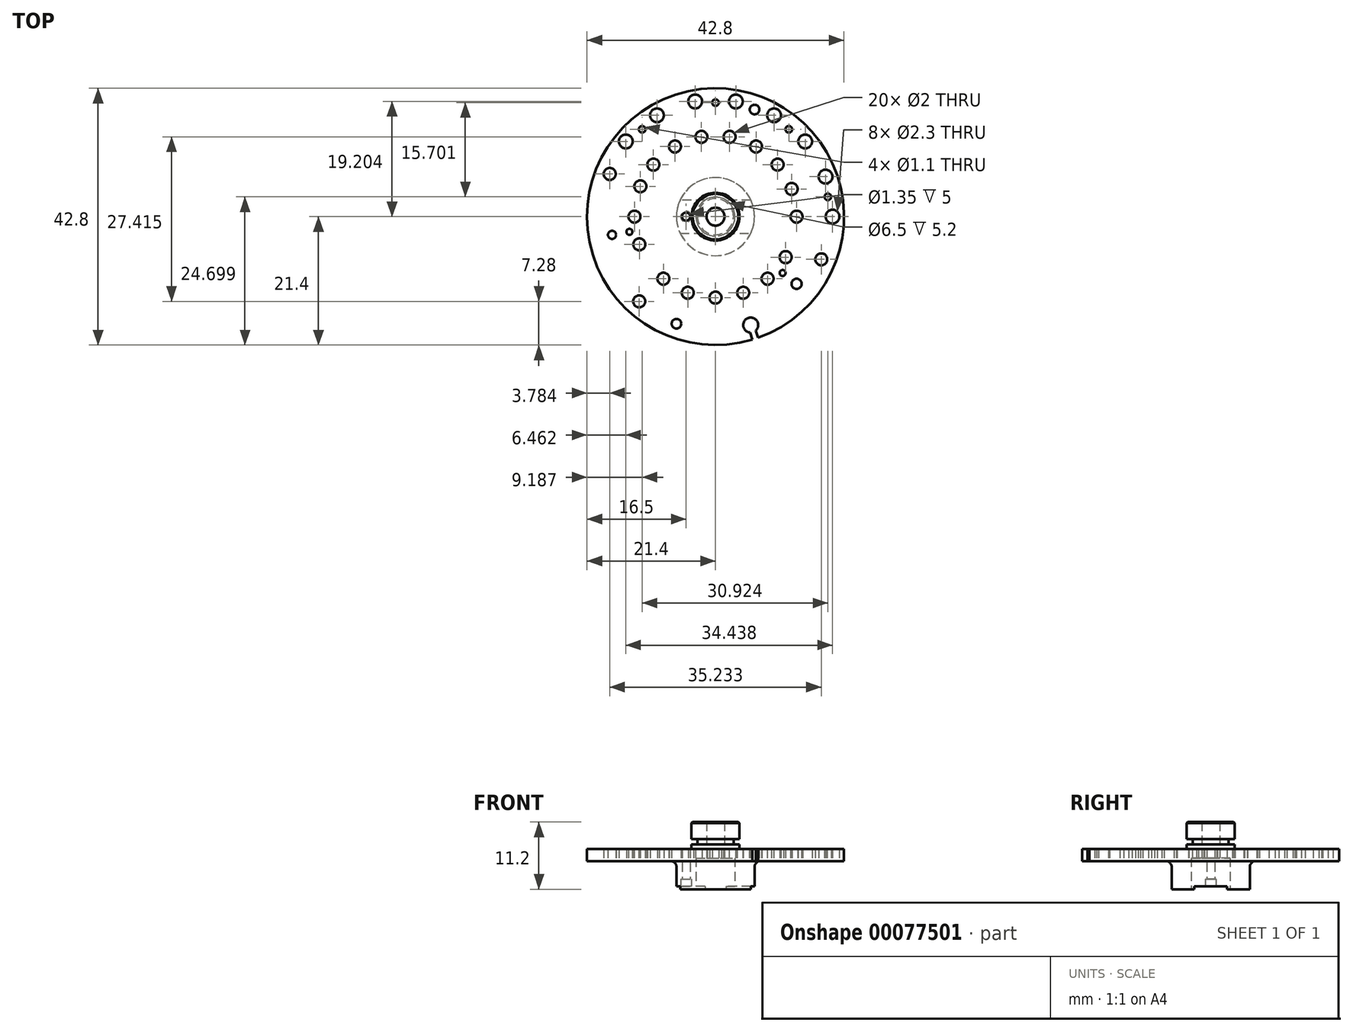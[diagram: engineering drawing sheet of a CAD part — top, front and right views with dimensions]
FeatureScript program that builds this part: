
annotation { "Feature Type Name" : "Feature", "Feature Type Description" : "" }
export const myFeature = defineFeature(function(context is Context, id is Id, definition is map)
    precondition{}
    {
        {
            var Q0;
            Q0=qCreatedBy(makeId("Front.planeOp"),FACE);
            var sketch = newSketch(context, id + "F0", { "sketchPlane" : qUnion([Q0])});
            skLineSegment(sketch, "E0", {"start": v(3.25, 0) * mm, "end": v(6.5, 0) * mm});
            skLineSegment(sketch, "E1", {"start": v(6.5, 0) * mm, "end": v(6.5, 4.7) * mm});
            skLineSegment(sketch, "E2", {"start": v(6.5, 4.7) * mm, "end": v(21.4, 4.7) * mm});
            skLineSegment(sketch, "E3", {"start": v(21.4, 4.7) * mm, "end": v(21.4, 6.7) * mm});
            skLineSegment(sketch, "E4", {"start": v(21.4, 6.7) * mm, "end": v(4, 6.7) * mm});
            skLineSegment(sketch, "E5", {"start": v(4, 6.7) * mm, "end": v(4, 7.5) * mm});
            skLineSegment(sketch, "E6", {"start": v(4, 11.2) * mm, "end": v(1.5, 11.2) * mm});
            skLineSegment(sketch, "E7", {"start": v(1.5, 11.2) * mm, "end": v(1.5, 5.2) * mm});
            skLineSegment(sketch, "E8", {"start": v(1.5, 5.2) * mm, "end": v(3.25, 5.2) * mm});
            skLineSegment(sketch, "E9", {"start": v(3.25, 5.2) * mm, "end": v(3.25, 0) * mm});
            skLineSegment(sketch, "E10", {"start": v(4, 7.5) * mm, "end": v(3, 7.5) * mm});
            skLineSegment(sketch, "E11", {"start": v(3, 7.5) * mm, "end": v(3, 8.35) * mm});
            skLineSegment(sketch, "E12", {"start": v(3, 8.35) * mm, "end": v(4, 8.35) * mm});
            skLineSegment(sketch, "E13", {"start": v(4, 8.35) * mm, "end": v(4, 11.2) * mm});
            skLineSegment(sketch, "E14", {"start": v(0, 0) * mm, "end": v(0, 11.2) * mm, "construction": true});
            skSolve(sketch);
        }
        {
            var Q0;
            Q0=makeQuery(id+"F0.imprint","IMPRINT",FACE,{"disambiguationData":[TD([[makeQuery(id+"F0.imprint","IMPRINT",EDGE,{"derivedFrom":sQuery(id+"F0.wireOp",EDGE,"E0")}),1.0]])]});
            var Q1;
            Q1=sQuery(id+"F0.wireOp",EDGE,"E14");
            revolve(context, id + "F1", {"entities" : qUnion([Q0]), "axis" : qUnion([Q1]), "revolveType" : RevolveType.FULL});
        }
        {
            var Q0;
            Q0=makeQuery(id+"F1.opRevolve","SWEPT_FACE",FACE,{"disambiguationData":[OSD([sQuery(id+"F0.wireOp",EDGE,"E2")])]});
            var sketch = newSketch(context, id + "F2", { "sketchPlane" : qUnion([Q0]), "disableImprinting" : false});
            skLineSegment(sketch, "E15", {"start": v(21.4, 0) * mm, "end": v(0, 0) * mm, "construction": true});
            skLineSegment(sketch, "E16", {"start": v(0, 0) * mm, "end": v(20.1, -7.32) * mm, "construction": true});
            skLineSegment(sketch, "E17", {"start": v(0, 0) * mm, "end": v(16.4, -13.76) * mm, "construction": true});
            skLineSegment(sketch, "E18", {"start": v(0, 0) * mm, "end": v(10.7, -18.53) * mm, "construction": true});
            skLineSegment(sketch, "E19", {"start": v(0, 0) * mm, "end": v(3.72, -21.07) * mm, "construction": true});
            skLineSegment(sketch, "E20", {"start": v(0, 0) * mm, "end": v(-3.72, -21.07) * mm, "construction": true});
            skLineSegment(sketch, "E21", {"start": v(0, 0) * mm, "end": v(-10.7, -18.53) * mm, "construction": true});
            skLineSegment(sketch, "E22", {"start": v(0, 0) * mm, "end": v(-16.4, -13.76) * mm, "construction": true});
            skLineSegment(sketch, "E23", {"start": v(0, 0) * mm, "end": v(-19.84, -8.02) * mm, "construction": true});
            skLineSegment(sketch, "E24", {"start": v(0, 0) * mm, "end": v(-21.4, 0) * mm, "construction": true});
            skLineSegment(sketch, "E25", {"start": v(0, 0) * mm, "end": v(-20.1, 7.32) * mm, "construction": true});
            skLineSegment(sketch, "E26", {"start": v(0, 0) * mm, "end": v(18.53, 10.7) * mm, "construction": true});
            skLineSegment(sketch, "E27", {"start": v(0, 0) * mm, "end": v(13.76, 16.4) * mm, "construction": true});
            skLineSegment(sketch, "E28", {"start": v(0, 0) * mm, "end": v(7.32, 20.1) * mm, "construction": true});
            skLineSegment(sketch, "E29", {"start": v(0, 0) * mm, "end": v(0, 21.4) * mm, "construction": true});
            skLineSegment(sketch, "E30", {"start": v(0, 0) * mm, "end": v(-7.32, 20.1) * mm, "construction": true});
            skLineSegment(sketch, "E31", {"start": v(0, 0) * mm, "end": v(-13.76, 16.4) * mm, "construction": true});
            skCircle(sketch, "E32", {"center": v(0, 0) * mm, "radius": 19.5 * mm, "construction": true});
            skCircle(sketch, "E33", {"center": v(0, 0) * mm, "radius": 13.5 * mm, "construction": true});
            skCircle(sketch, "E34", {"center": v(19.5, 0) * mm, "radius": 1.15 * mm});
            skCircle(sketch, "E35", {"center": v(18.32, -6.67) * mm, "radius": 1.15 * mm});
            skCircle(sketch, "E36", {"center": v(14.94, -12.53) * mm, "radius": 1.15 * mm});
            skCircle(sketch, "E37", {"center": v(9.75, -16.89) * mm, "radius": 1.15 * mm});
            skCircle(sketch, "E38", {"center": v(3.39, -19.2) * mm, "radius": 1.15 * mm});
            skCircle(sketch, "E39", {"center": v(-3.39, -19.2) * mm, "radius": 1.15 * mm});
            skCircle(sketch, "E40", {"center": v(-9.75, -16.89) * mm, "radius": 1.15 * mm});
            skCircle(sketch, "E41", {"center": v(-14.94, -12.53) * mm, "radius": 1.15 * mm});
            skCircle(sketch, "E42", {"center": v(-17.62, -7.12) * mm, "radius": 1 * mm});
            skCircle(sketch, "E43", {"center": v(11.7, 6.75) * mm, "radius": 1 * mm});
            skCircle(sketch, "E44", {"center": v(8.68, 10.34) * mm, "radius": 1 * mm});
            skCircle(sketch, "E45", {"center": v(12.69, -4.62) * mm, "radius": 1 * mm});
            skCircle(sketch, "E46", {"center": v(13.5, 0) * mm, "radius": 1 * mm});
            skCircle(sketch, "E47", {"center": v(10.34, -8.68) * mm, "radius": 1 * mm});
            skCircle(sketch, "E48", {"center": v(6.75, -11.7) * mm, "radius": 1 * mm});
            skCircle(sketch, "E49", {"center": v(2.34, -13.3) * mm, "radius": 1 * mm});
            skCircle(sketch, "E50", {"center": v(-2.34, -13.3) * mm, "radius": 1 * mm});
            skCircle(sketch, "E51", {"center": v(-6.75, -11.7) * mm, "radius": 1 * mm});
            skCircle(sketch, "E52", {"center": v(-10.34, -8.68) * mm, "radius": 1 * mm});
            skCircle(sketch, "E53", {"center": v(-12.52, -5.06) * mm, "radius": 1 * mm});
            skCircle(sketch, "E54", {"center": v(-13.5, 0) * mm, "radius": 1 * mm});
            skCircle(sketch, "E55", {"center": v(-12.69, 4.62) * mm, "radius": 1 * mm});
            skCircle(sketch, "E56", {"center": v(-8.68, 10.34) * mm, "radius": 1 * mm});
            skCircle(sketch, "E57", {"center": v(-4.62, 12.69) * mm, "radius": 1 * mm});
            skCircle(sketch, "E58", {"center": v(0, 13.5) * mm, "radius": 1 * mm});
            skCircle(sketch, "E59", {"center": v(4.62, 12.69) * mm, "radius": 1 * mm});
            skLineSegment(sketch, "E60", {"start": v(0, 0) * mm, "end": v(21.07, -3.72) * mm, "construction": true});
            skLineSegment(sketch, "E61", {"start": v(0, 0) * mm, "end": v(13.76, -16.4) * mm, "construction": true});
            skLineSegment(sketch, "E62", {"start": v(0, 0) * mm, "end": v(7.32, -20.1) * mm, "construction": true});
            skLineSegment(sketch, "E63", {"start": v(0, 0) * mm, "end": v(0, -21.4) * mm, "construction": true});
            skLineSegment(sketch, "E64", {"start": v(0, 0) * mm, "end": v(-13.76, -16.4) * mm, "construction": true});
            skCircle(sketch, "E65", {"center": v(18.71, -3.3) * mm, "radius": 0.55 * mm});
            skCircle(sketch, "E66", {"center": v(12.21, -14.55) * mm, "radius": 0.55 * mm});
            skCircle(sketch, "E67", {"center": v(0, -19) * mm, "radius": 0.55 * mm});
            skCircle(sketch, "E68", {"center": v(-12.21, -14.55) * mm, "radius": 0.55 * mm});
            skCircle(sketch, "E69", {"center": v(6.5, -17.85) * mm, "radius": 0.8 * mm});
            skCircle(sketch, "E70", {"center": v(0, 0) * mm, "radius": 19 * mm, "construction": true});
            skLineSegment(sketch, "E71", {"start": v(0, 0) * mm, "end": v(17.62, 7.12) * mm, "construction": true});
            skCircle(sketch, "E72", {"center": v(17.62, 7.12) * mm, "radius": 1 * mm});
            skLineSegment(sketch, "E73", {"start": v(0, 0) * mm, "end": v(5.87, 18.07) * mm, "construction": true});
            skArc(sketch, "E74", {"start": v(5.75, 19.31) * mm, "mid": v(5.49, 16.88) * mm, "end": v(6.7, 19) * mm});
            skLineSegment(sketch, "E75", {"start": v(5.75, 19.31) * mm, "end": v(6.14, 20.5) * mm});
            skLineSegment(sketch, "E76", {"start": v(6.7, 19) * mm, "end": v(7.09, 20.2) * mm});
            skCircle(sketch, "E77", {"center": v(13.5, 11.2) * mm, "radius": 0.85 * mm});
            skCircle(sketch, "E78", {"center": v(11.18, 9.38) * mm, "radius": 0.5 * mm});
            skLineSegment(sketch, "E79", {"start": v(11.18, 9.38) * mm, "end": v(0, 0) * mm, "construction": true});
            skCircle(sketch, "E80", {"center": v(-6.5, 17.85) * mm, "radius": 0.8 * mm});
            skCircle(sketch, "E81", {"center": v(-12.71, 14.12) * mm, "radius": 1 * mm});
            skLineSegment(sketch, "E82", {"start": v(0, 0) * mm, "end": v(-12.71, 14.12) * mm, "construction": true});
            skLineSegment(sketch, "E83", {"start": v(0, 0) * mm, "end": v(-17.23, 3.04) * mm, "construction": true});
            skPoint(sketch, "E84", {"position": v(-14.33, 2.53) * mm});
            skCircle(sketch, "E85", {"center": v(-17.23, 3.04) * mm, "radius": 0.68 * mm});
            skCircle(sketch, "E86", {"center": v(-14.33, 2.53) * mm, "radius": 0.5 * mm});
            skSolve(sketch);
        }
        {
            var Q0;
            {Q0=qUnion([makeQuery(id+"F2.imprint","IMPRINT",FACE,{"disambiguationData":[TD([[makeQuery(id+"F2.imprint","IMPRINT",EDGE,{"derivedFrom":sQuery(id+"F2.wireOp",EDGE,"E34")}),1.0]])]}),makeQuery(id+"F2.imprint","IMPRINT",FACE,{"disambiguationData":[TD([[makeQuery(id+"F2.imprint","IMPRINT",EDGE,{"derivedFrom":sQuery(id+"F2.wireOp",EDGE,"E35")}),1.0]])]}),makeQuery(id+"F2.imprint","IMPRINT",FACE,{"disambiguationData":[TD([[makeQuery(id+"F2.imprint","IMPRINT",EDGE,{"derivedFrom":sQuery(id+"F2.wireOp",EDGE,"E36")}),1.0]])]}),makeQuery(id+"F2.imprint","IMPRINT",FACE,{"disambiguationData":[TD([[makeQuery(id+"F2.imprint","IMPRINT",EDGE,{"derivedFrom":sQuery(id+"F2.wireOp",EDGE,"E37")}),1.0]])]}),makeQuery(id+"F2.imprint","IMPRINT",FACE,{"disambiguationData":[TD([[makeQuery(id+"F2.imprint","IMPRINT",EDGE,{"derivedFrom":sQuery(id+"F2.wireOp",EDGE,"E38")}),1.0]])]}),makeQuery(id+"F2.imprint","IMPRINT",FACE,{"disambiguationData":[TD([[makeQuery(id+"F2.imprint","IMPRINT",EDGE,{"derivedFrom":sQuery(id+"F2.wireOp",EDGE,"E39")}),1.0]])]}),makeQuery(id+"F2.imprint","IMPRINT",FACE,{"disambiguationData":[TD([[makeQuery(id+"F2.imprint","IMPRINT",EDGE,{"derivedFrom":sQuery(id+"F2.wireOp",EDGE,"E40")}),1.0]])]}),makeQuery(id+"F2.imprint","IMPRINT",FACE,{"disambiguationData":[TD([[makeQuery(id+"F2.imprint","IMPRINT",EDGE,{"derivedFrom":sQuery(id+"F2.wireOp",EDGE,"E41")}),1.0]])]}),makeQuery(id+"F2.imprint","IMPRINT",FACE,{"disambiguationData":[TD([[makeQuery(id+"F2.imprint","IMPRINT",EDGE,{"derivedFrom":sQuery(id+"F2.wireOp",EDGE,"E42")}),1.0]])]}),makeQuery(id+"F2.imprint","IMPRINT",FACE,{"disambiguationData":[TD([[makeQuery(id+"F2.imprint","IMPRINT",EDGE,{"derivedFrom":sQuery(id+"F2.wireOp",EDGE,"E43")}),1.0]])]}),makeQuery(id+"F2.imprint","IMPRINT",FACE,{"disambiguationData":[TD([[makeQuery(id+"F2.imprint","IMPRINT",EDGE,{"derivedFrom":sQuery(id+"F2.wireOp",EDGE,"E44")}),1.0]])]}),makeQuery(id+"F2.imprint","IMPRINT",FACE,{"disambiguationData":[TD([[makeQuery(id+"F2.imprint","IMPRINT",EDGE,{"derivedFrom":sQuery(id+"F2.wireOp",EDGE,"E45")}),1.0]])]}),makeQuery(id+"F2.imprint","IMPRINT",FACE,{"disambiguationData":[TD([[makeQuery(id+"F2.imprint","IMPRINT",EDGE,{"derivedFrom":sQuery(id+"F2.wireOp",EDGE,"E46")}),1.0]])]}),makeQuery(id+"F2.imprint","IMPRINT",FACE,{"disambiguationData":[TD([[makeQuery(id+"F2.imprint","IMPRINT",EDGE,{"derivedFrom":sQuery(id+"F2.wireOp",EDGE,"E47")}),1.0]])]}),makeQuery(id+"F2.imprint","IMPRINT",FACE,{"disambiguationData":[TD([[makeQuery(id+"F2.imprint","IMPRINT",EDGE,{"derivedFrom":sQuery(id+"F2.wireOp",EDGE,"E48")}),1.0]])]}),makeQuery(id+"F2.imprint","IMPRINT",FACE,{"disambiguationData":[TD([[makeQuery(id+"F2.imprint","IMPRINT",EDGE,{"derivedFrom":sQuery(id+"F2.wireOp",EDGE,"E49")}),1.0]])]}),makeQuery(id+"F2.imprint","IMPRINT",FACE,{"disambiguationData":[TD([[makeQuery(id+"F2.imprint","IMPRINT",EDGE,{"derivedFrom":sQuery(id+"F2.wireOp",EDGE,"E50")}),1.0]])]}),makeQuery(id+"F2.imprint","IMPRINT",FACE,{"disambiguationData":[TD([[makeQuery(id+"F2.imprint","IMPRINT",EDGE,{"derivedFrom":sQuery(id+"F2.wireOp",EDGE,"E51")}),1.0]])]}),makeQuery(id+"F2.imprint","IMPRINT",FACE,{"disambiguationData":[TD([[makeQuery(id+"F2.imprint","IMPRINT",EDGE,{"derivedFrom":sQuery(id+"F2.wireOp",EDGE,"E52")}),1.0]])]}),makeQuery(id+"F2.imprint","IMPRINT",FACE,{"disambiguationData":[TD([[makeQuery(id+"F2.imprint","IMPRINT",EDGE,{"derivedFrom":sQuery(id+"F2.wireOp",EDGE,"E53")}),1.0]])]}),makeQuery(id+"F2.imprint","IMPRINT",FACE,{"disambiguationData":[TD([[makeQuery(id+"F2.imprint","IMPRINT",EDGE,{"derivedFrom":sQuery(id+"F2.wireOp",EDGE,"E54")}),1.0]])]}),makeQuery(id+"F2.imprint","IMPRINT",FACE,{"disambiguationData":[TD([[makeQuery(id+"F2.imprint","IMPRINT",EDGE,{"derivedFrom":sQuery(id+"F2.wireOp",EDGE,"E55")}),1.0]])]}),makeQuery(id+"F2.imprint","IMPRINT",FACE,{"disambiguationData":[TD([[makeQuery(id+"F2.imprint","IMPRINT",EDGE,{"derivedFrom":sQuery(id+"F2.wireOp",EDGE,"E56")}),1.0]])]}),makeQuery(id+"F2.imprint","IMPRINT",FACE,{"disambiguationData":[TD([[makeQuery(id+"F2.imprint","IMPRINT",EDGE,{"derivedFrom":sQuery(id+"F2.wireOp",EDGE,"E57")}),1.0]])]}),makeQuery(id+"F2.imprint","IMPRINT",FACE,{"disambiguationData":[TD([[makeQuery(id+"F2.imprint","IMPRINT",EDGE,{"derivedFrom":sQuery(id+"F2.wireOp",EDGE,"E58")}),1.0]])]}),makeQuery(id+"F2.imprint","IMPRINT",FACE,{"disambiguationData":[TD([[makeQuery(id+"F2.imprint","IMPRINT",EDGE,{"derivedFrom":sQuery(id+"F2.wireOp",EDGE,"E59")}),1.0]])]}),makeQuery(id+"F2.imprint","IMPRINT",FACE,{"disambiguationData":[TD([[makeQuery(id+"F2.imprint","IMPRINT",EDGE,{"derivedFrom":sQuery(id+"F2.wireOp",EDGE,"E65")}),1.0]])]}),makeQuery(id+"F2.imprint","IMPRINT",FACE,{"disambiguationData":[TD([[makeQuery(id+"F2.imprint","IMPRINT",EDGE,{"derivedFrom":sQuery(id+"F2.wireOp",EDGE,"E66")}),1.0]])]}),makeQuery(id+"F2.imprint","IMPRINT",FACE,{"disambiguationData":[TD([[makeQuery(id+"F2.imprint","IMPRINT",EDGE,{"derivedFrom":sQuery(id+"F2.wireOp",EDGE,"E67")}),1.0]])]}),makeQuery(id+"F2.imprint","IMPRINT",FACE,{"disambiguationData":[TD([[makeQuery(id+"F2.imprint","IMPRINT",EDGE,{"derivedFrom":sQuery(id+"F2.wireOp",EDGE,"E68")}),1.0]])]}),makeQuery(id+"F2.imprint","IMPRINT",FACE,{"disambiguationData":[TD([[makeQuery(id+"F2.imprint","IMPRINT",EDGE,{"derivedFrom":sQuery(id+"F2.wireOp",EDGE,"E69")}),1.0]])]}),makeQuery(id+"F2.imprint","IMPRINT",FACE,{"disambiguationData":[TD([[makeQuery(id+"F2.imprint","IMPRINT",EDGE,{"derivedFrom":sQuery(id+"F2.wireOp",EDGE,"E72")}),1.0]])]}),makeQuery(id+"F2.imprint","IMPRINT",FACE,{"disambiguationData":[TD([[makeQuery(id+"F2.imprint","IMPRINT",EDGE,{"derivedFrom":sQuery(id+"F2.wireOp",EDGE,"E77")}),1.0]])]}),makeQuery(id+"F2.imprint","IMPRINT",FACE,{"disambiguationData":[TD([[makeQuery(id+"F2.imprint","IMPRINT",EDGE,{"derivedFrom":sQuery(id+"F2.wireOp",EDGE,"E78")}),1.0]])]}),makeQuery(id+"F2.imprint","IMPRINT",FACE,{"disambiguationData":[TD([[makeQuery(id+"F2.imprint","IMPRINT",EDGE,{"derivedFrom":sQuery(id+"F2.wireOp",EDGE,"E80")}),1.0]])]}),makeQuery(id+"F2.imprint","IMPRINT",FACE,{"disambiguationData":[TD([[makeQuery(id+"F2.imprint","IMPRINT",EDGE,{"derivedFrom":sQuery(id+"F2.wireOp",EDGE,"E81")}),1.0]])]}),makeQuery(id+"F2.imprint","IMPRINT",FACE,{"disambiguationData":[TD([[makeQuery(id+"F2.imprint","IMPRINT",EDGE,{"derivedFrom":sQuery(id+"F2.wireOp",EDGE,"E85")}),1.0]])]}),makeQuery(id+"F2.imprint","IMPRINT",FACE,{"disambiguationData":[TD([[makeQuery(id+"F2.imprint","IMPRINT",EDGE,{"derivedFrom":sQuery(id+"F2.wireOp",EDGE,"E86")}),1.0]])]})]);}
            var Q1;
            Q1=makeQuery(id+"F2.imprint","IMPRINT",FACE,{"disambiguationData":[TD([[makeQuery(id+"F2.imprint","IMPRINT",EDGE,{"derivedFrom":sQuery(id+"F2.wireOp",EDGE,"E74")}),1.0]])]});
            extrude(context, id + "F3", {"entities" : qUnion([Q0, Q1]), "operationType" : NewBodyOperationType.REMOVE, "endBound" : BoundingType.THROUGH_ALL, "oppositeDirection" : true, "depth" : 25 * mm});
        }
        {
            var Q0;
            Q0=makeQuery(id+"F1.opRevolve","SWEPT_EDGE",EDGE,{"disambiguationData":[OSD([sQuery(id+"F0.wireOp",EDGE,"E1"),sQuery(id+"F0.wireOp",EDGE,"E2")])]});
            fillet(context, id + "F4", {"entities" : qUnion([Q0]), "radius" : 1 * mm, "tangentPropagation" : true, "allowEdgeOverflow" : false});
        }
        {
            var Q0;
            Q0=makeQuery(id+"F1.opRevolve","SWEPT_EDGE",EDGE,{"disambiguationData":[OSD([sQuery(id+"F0.wireOp",EDGE,"E4"),sQuery(id+"F0.wireOp",EDGE,"E5")])]});
            fillet(context, id + "F5", {"entities" : qUnion([Q0]), "radius" : 0.2 * mm, "tangentPropagation" : true, "allowEdgeOverflow" : false});
        }
        {
            var Q0;
            Q0=makeQuery(id+"F1.opRevolve","SWEPT_EDGE",EDGE,{"disambiguationData":[OSD([sQuery(id+"F0.wireOp",EDGE,"E6"),sQuery(id+"F0.wireOp",EDGE,"E13")])]});
            chamfer(context, id + "F6", {"entities" : qUnion([Q0]), "width" : 0.2 * mm, "tangentPropagation" : true});
        }
        {
            var Q0;
            Q0=makeQuery(id+"F1.opRevolve","SWEPT_FACE",FACE,{"disambiguationData":[OSD([sQuery(id+"F0.wireOp",EDGE,"E0")])]});
            var sketch = newSketch(context, id + "F7", { "sketchPlane" : qUnion([Q0])});
            skLineSegment(sketch, "E87", {"start": v(5.89, -2.75) * mm, "end": v(-5.89, -2.75) * mm});
            skLineSegment(sketch, "E88", {"start": v(-5.89, 2.75) * mm, "end": v(5.89, 2.75) * mm});
            skSolve(sketch);
        }
        {
            var Q0;
            {var subQ0=sQuery(id+"F0.wireOp",EDGE,"E0");var subQ4=sQuery(id+"F7.wireOp",EDGE,"E87");var subQ6=makeQuery(id+"F1.opRevolve","SWEPT_EDGE",EDGE,{"disambiguationData":[OSD([subQ0,sQuery(id+"F0.wireOp",EDGE,"E1")])]});var subQ8=makeQuery(id+"F7.imprint","INTERSECT",VERTEX,{"disambiguationData":[OD(0.0)],"derivedFrom":[subQ6,subQ4]});Q0=makeQuery(id+"F7.imprint","IMPRINT",FACE,{"disambiguationData":[TD([[makeQuery(id+"F7.imprint","IMPRINT",EDGE,{"disambiguationData":[TD([[subQ8,-1.0]])],"derivedFrom":subQ4}),-1.0]])]});}
            var Q1;
            {var subQ0=sQuery(id+"F0.wireOp",EDGE,"E0");var subQ4=sQuery(id+"F7.wireOp",EDGE,"E87");var subQ6=makeQuery(id+"F1.opRevolve","SWEPT_EDGE",EDGE,{"disambiguationData":[OSD([subQ0,sQuery(id+"F0.wireOp",EDGE,"E1")])]});var subQ8=makeQuery(id+"F7.imprint","INTERSECT",VERTEX,{"disambiguationData":[OD(1.0)],"derivedFrom":[subQ6,subQ4]});Q1=makeQuery(id+"F7.imprint","IMPRINT",FACE,{"disambiguationData":[TD([[makeQuery(id+"F7.imprint","IMPRINT",EDGE,{"disambiguationData":[TD([[subQ8,1.0]])],"derivedFrom":subQ4}),-1.0]])]});}
            extrude(context, id + "F8", {"entities" : qUnion([Q0, Q1]), "operationType" : NewBodyOperationType.REMOVE, "oppositeDirection" : true, "depth" : 0.5 * mm});
        }
        {
            var Q0;
            {var subQ0=sQuery(id+"F0.wireOp",EDGE,"E0");var subQ1=sQuery(id+"F0.wireOp",EDGE,"E1");var subQ2=sQuery(id+"F0.wireOp",EDGE,"E9");var subQ3=sQuery(id+"F7.wireOp",EDGE,"E87");var subQ4=sQuery(id+"F7.wireOp",EDGE,"E88");var subQ5=makeQuery(id+"F1.opRevolve","SWEPT_EDGE",EDGE,{"disambiguationData":[OSD([subQ0,subQ2])]});var subQ6=makeQuery(id+"F7.imprint","INTERSECT",VERTEX,{"disambiguationData":[OD(1.0)],"derivedFrom":[subQ5,subQ3]});var subQ7=makeQuery(id+"F1.opRevolve","SWEPT_EDGE",EDGE,{"disambiguationData":[OSD([subQ0,subQ1])]});var subQ8=makeQuery(id+"F7.imprint","INTERSECT",VERTEX,{"disambiguationData":[OD(1.0)],"derivedFrom":[subQ7,subQ3]});var subQ10=makeQuery(id+"F7.imprint","INTERSECT",VERTEX,{"disambiguationData":[OD(0.0)],"derivedFrom":[subQ7,subQ4]});Q0=makeQuery(id+"F8.boolean.opBoolean","COPY",FACE,{"derivedFrom":makeQuery(id+"F8.opExtrude","CAP_FACE",FACE,{"disambiguationData":[OSD([subQ0,subQ1,subQ2,subQ3,subQ4]),TDD([makeQuery(id+"F7.imprint","IMPRINT",EDGE,{"disambiguationData":[TD([[subQ8,1.0]])],"derivedFrom":subQ3}),makeQuery(id+"F7.imprint","IMPRINT",EDGE,{"disambiguationData":[TD([[subQ10,-1.0]])],"derivedFrom":subQ4}),makeQuery(id+"F7.imprint","IMPRINT",EDGE,{"disambiguationData":[TD([[subQ8,1.0]])],"derivedFrom":subQ7}),makeQuery(id+"F7.imprint","IMPRINT",EDGE,{"disambiguationData":[TD([[subQ6,1.0]])],"derivedFrom":subQ5})])],"isStart":false})});}
            var sketch = newSketch(context, id + "F9", { "sketchPlane" : qUnion([Q0])});
            skCircle(sketch, "E89", {"center": v(-4.9, 0) * mm, "radius": 0.68 * mm});
            skSolve(sketch);
        }
        {
            var Q0;
            Q0=makeQuery(id+"F9.imprint","IMPRINT",FACE,{"disambiguationData":[TD([[makeQuery(id+"F9.imprint","IMPRINT",EDGE,{"derivedFrom":sQuery(id+"F9.wireOp",EDGE,"E89")}),1.0]])]});
            extrude(context, id + "F10", {"entities" : qUnion([Q0]), "operationType" : NewBodyOperationType.REMOVE, "endBound" : BoundingType.THROUGH_ALL, "oppositeDirection" : true, "depth" : 25 * mm});
        }
        {
            var Q0;
            {var subQ0=sQuery(id+"F0.wireOp",EDGE,"E0");var subQ1=sQuery(id+"F0.wireOp",EDGE,"E1");var subQ2=sQuery(id+"F0.wireOp",EDGE,"E9");var subQ3=sQuery(id+"F7.wireOp",EDGE,"E87");var subQ4=sQuery(id+"F7.wireOp",EDGE,"E88");var subQ5=makeQuery(id+"F1.opRevolve","SWEPT_EDGE",EDGE,{"disambiguationData":[OSD([subQ0,subQ2])]});var subQ6=makeQuery(id+"F7.imprint","INTERSECT",VERTEX,{"disambiguationData":[OD(1.0)],"derivedFrom":[subQ5,subQ3]});var subQ7=makeQuery(id+"F1.opRevolve","SWEPT_EDGE",EDGE,{"disambiguationData":[OSD([subQ0,subQ1])]});var subQ8=makeQuery(id+"F7.imprint","INTERSECT",VERTEX,{"disambiguationData":[OD(1.0)],"derivedFrom":[subQ7,subQ3]});var subQ10=makeQuery(id+"F7.imprint","INTERSECT",VERTEX,{"disambiguationData":[OD(0.0)],"derivedFrom":[subQ7,subQ4]});Q0=makeQuery(id+"F8.boolean.opBoolean","COPY",FACE,{"derivedFrom":makeQuery(id+"F8.opExtrude","CAP_FACE",FACE,{"disambiguationData":[OSD([subQ0,subQ1,subQ2,subQ3,subQ4]),TDD([makeQuery(id+"F7.imprint","IMPRINT",EDGE,{"disambiguationData":[TD([[subQ8,1.0]])],"derivedFrom":subQ3}),makeQuery(id+"F7.imprint","IMPRINT",EDGE,{"disambiguationData":[TD([[subQ10,-1.0]])],"derivedFrom":subQ4}),makeQuery(id+"F7.imprint","IMPRINT",EDGE,{"disambiguationData":[TD([[subQ8,1.0]])],"derivedFrom":subQ7}),makeQuery(id+"F7.imprint","IMPRINT",EDGE,{"disambiguationData":[TD([[subQ6,1.0]])],"derivedFrom":subQ5})])],"isStart":false})});}
            var sketch = newSketch(context, id + "F11", { "sketchPlane" : qUnion([Q0])});
            skCircle(sketch, "E90", {"center": v(-4.9, 0) * mm, "radius": 0.9 * mm});
            skSolve(sketch);
        }
        {
            var Q0;
            {var subQ0=makeQuery(id+"F11.imprint","IMPRINT",EDGE,{"derivedFrom":makeQuery(id+"F10.boolean.opBoolean","COPY",EDGE,{"derivedFrom":makeQuery(id+"F10.opExtrude","CAP_EDGE",EDGE,{"disambiguationData":[OSD([sQuery(id+"F9.wireOp",EDGE,"E89")])],"isStart":true})})});Q0=qUnion([makeQuery(id+"F11.imprint","IMPRINT",FACE,{"disambiguationData":[TD([[subQ0,1.0]])]}),makeQuery(id+"F11.imprint","IMPRINT",FACE,{"disambiguationData":[TD([[makeQuery(id+"F11.imprint","IMPRINT",EDGE,{"derivedFrom":sQuery(id+"F11.wireOp",EDGE,"E90")}),1.0]])]})]);}
            extrude(context, id + "F12", {"entities" : qUnion([Q0]), "operationType" : NewBodyOperationType.REMOVE, "oppositeDirection" : true, "depth" : 1.2 * mm});
        }
    });
